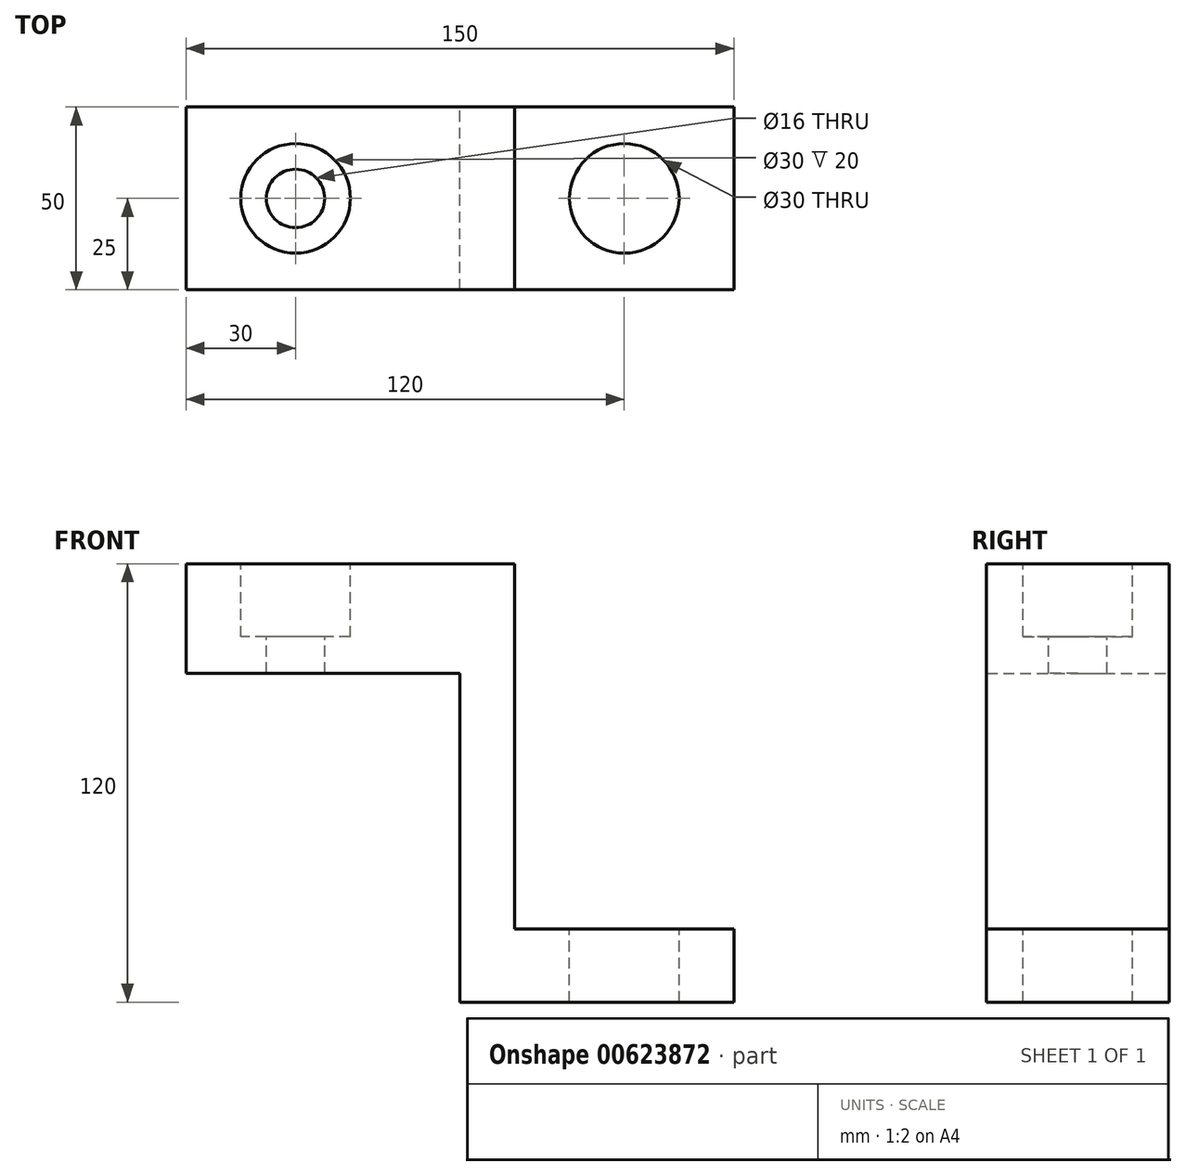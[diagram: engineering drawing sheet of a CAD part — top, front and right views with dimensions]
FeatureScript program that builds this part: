
annotation { "Feature Type Name" : "Feature", "Feature Type Description" : "" }
export const myFeature = defineFeature(function(context is Context, id is Id, definition is map)
    precondition{}
    {
        {
            var Q0;
            Q0=qCreatedBy(makeId("Front.planeOp"),FACE);
            var sketch = newSketch(context, id + "F0", { "sketchPlane" : qUnion([Q0])});
            skLineSegment(sketch, "E0", {"start": v(-90, 100) * mm, "end": v(0, 100) * mm});
            skLineSegment(sketch, "E1", {"start": v(0, 100) * mm, "end": v(0, 0) * mm});
            skLineSegment(sketch, "E2", {"start": v(0, 0) * mm, "end": v(60, 0) * mm});
            skLineSegment(sketch, "E3", {"start": v(60, 0) * mm, "end": v(60, -20) * mm});
            skLineSegment(sketch, "E4", {"start": v(60, -20) * mm, "end": v(-15, -20) * mm});
            skLineSegment(sketch, "E5", {"start": v(-15, -20) * mm, "end": v(-15, 70) * mm});
            skLineSegment(sketch, "E6", {"start": v(-15, 70) * mm, "end": v(-90, 70) * mm});
            skLineSegment(sketch, "E7", {"start": v(-90, 70) * mm, "end": v(-90, 100) * mm});
            skSolve(sketch);
        }
        {
            var Q0;
            Q0=makeQuery(id+"F0.imprint","IMPRINT",FACE,{"disambiguationData":[TD([[makeQuery(id+"F0.imprint","IMPRINT",EDGE,{"derivedFrom":sQuery(id+"F0.wireOp",EDGE,"E0")}),-1.0]])]});
            extrude(context, id + "F1", {"entities" : qUnion([Q0]), "depth" : 50 * mm, "offsetDistance" : 25 * mm});
        }
        {
            var Q0;
            Q0=makeQuery(id+"F1.opExtrude","SWEPT_FACE",FACE,{"disambiguationData":[OSD([sQuery(id+"F0.wireOp",EDGE,"E0")])]});
            var sketch = newSketch(context, id + "F2", { "sketchPlane" : qUnion([Q0])});
            skPoint(sketch, "E8", {"position": v(-60, -25) * mm});
            skSolve(sketch);
        }
        {
            var Q0;
            Q0=sQuery(id+"F2.wireOp",VERTEX,"E8");
            var Q1;
            Q1=makeQuery(id+"F1.opExtrude","SWEPT_BODY",BODY,{"disambiguationData":[OSD([sQuery(id+"F0.wireOp",EDGE,"E0"),sQuery(id+"F0.wireOp",EDGE,"E1"),sQuery(id+"F0.wireOp",EDGE,"E2"),sQuery(id+"F0.wireOp",EDGE,"E3"),sQuery(id+"F0.wireOp",EDGE,"E4"),sQuery(id+"F0.wireOp",EDGE,"E5"),sQuery(id+"F0.wireOp",EDGE,"E6"),sQuery(id+"F0.wireOp",EDGE,"E7")])]});
            hole(context, id + "F3", {"style" : HoleStyle.C_BORE, "endStyle" : HoleEndStyle.THROUGH, "holeDiameter" : 16 * mm, "cBoreDiameter" : 30 * mm, "cBoreDepth" : 20 * mm, "majorDiameter" : 5 * mm, "isTappedThrough" : true, "tappedDepth" : 12 * mm, "tapClearance" : 3, "locations" : qUnion([Q0]), "scope" : qUnion([Q1])});
        }
        {
            var Q0;
            Q0=makeQuery(id+"F1.opExtrude","SWEPT_FACE",FACE,{"disambiguationData":[OSD([sQuery(id+"F0.wireOp",EDGE,"E2")])]});
            var sketch = newSketch(context, id + "F4", { "sketchPlane" : qUnion([Q0])});
            skPoint(sketch, "E9", {"position": v(30, -25) * mm});
            skSolve(sketch);
        }
        {
            var Q0;
            Q0=sQuery(id+"F4.wireOp",VERTEX,"E9");
            var Q1;
            Q1=makeQuery(id+"F1.opExtrude","SWEPT_BODY",BODY,{"disambiguationData":[OSD([sQuery(id+"F0.wireOp",EDGE,"E0"),sQuery(id+"F0.wireOp",EDGE,"E1"),sQuery(id+"F0.wireOp",EDGE,"E2"),sQuery(id+"F0.wireOp",EDGE,"E3"),sQuery(id+"F0.wireOp",EDGE,"E4"),sQuery(id+"F0.wireOp",EDGE,"E5"),sQuery(id+"F0.wireOp",EDGE,"E6"),sQuery(id+"F0.wireOp",EDGE,"E7")])]});
            hole(context, id + "F5", {"style" : HoleStyle.C_BORE, "endStyle" : HoleEndStyle.THROUGH, "holeDiameter" : 30 * mm, "cBoreDiameter" : 30 * mm, "cBoreDepth" : 20 * mm, "majorDiameter" : 5 * mm, "isTappedThrough" : true, "tappedDepth" : 12 * mm, "tapClearance" : 3, "locations" : qUnion([Q0]), "scope" : qUnion([Q1])});
        }
    });
